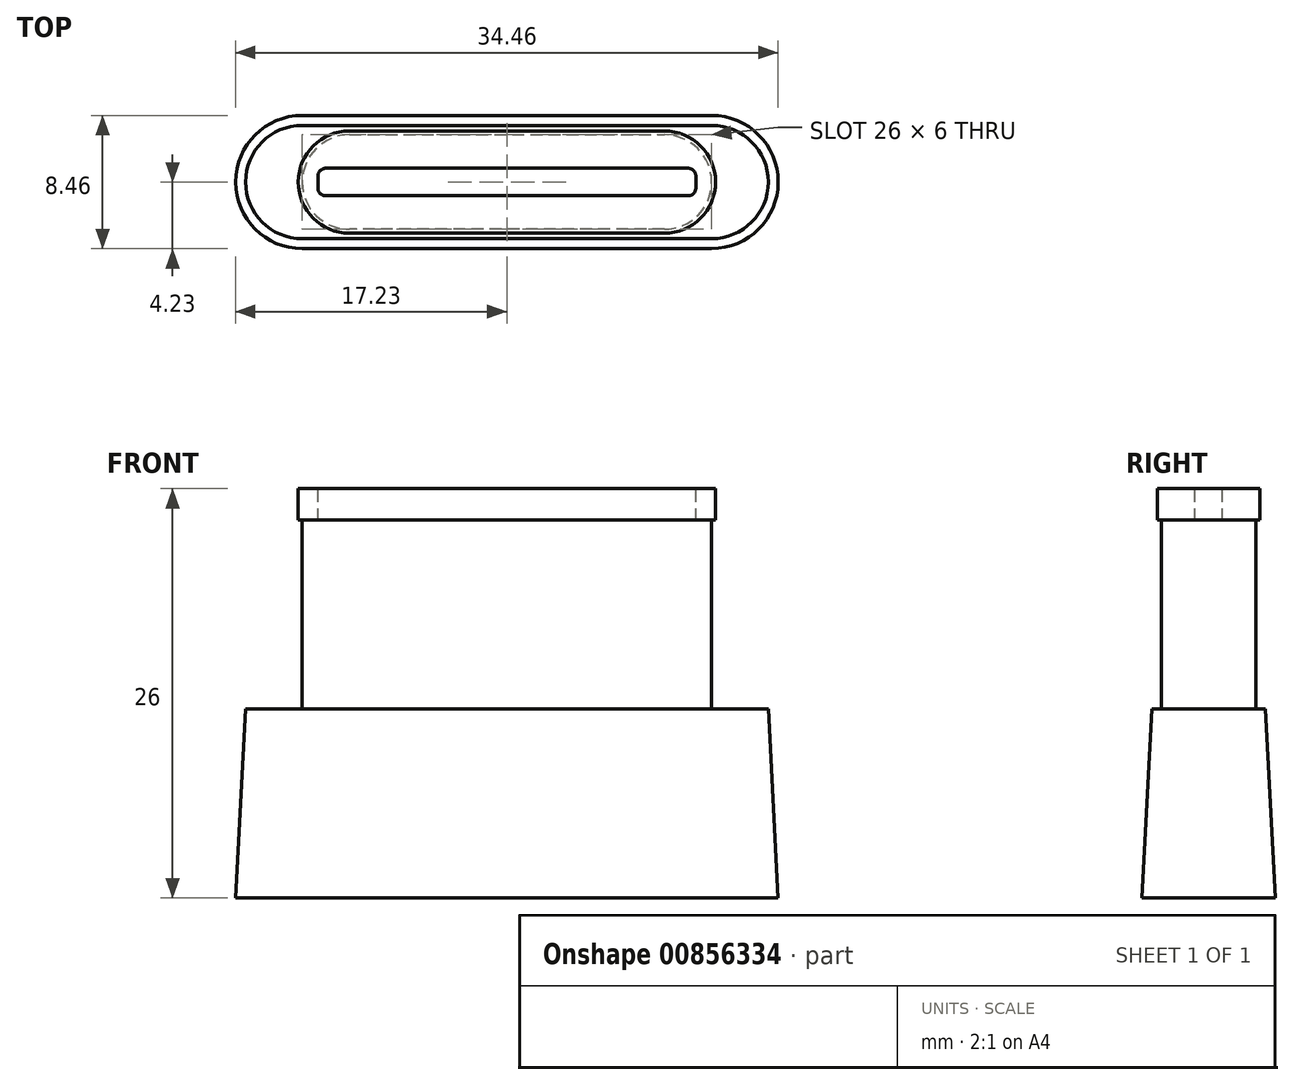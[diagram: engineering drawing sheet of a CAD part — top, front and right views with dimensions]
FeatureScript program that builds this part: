
annotation { "Feature Type Name" : "Feature", "Feature Type Description" : "" }
export const myFeature = defineFeature(function(context is Context, id is Id, definition is map)
    precondition{}
    {
        {
            var Q0;
            Q0=qCreatedBy(makeId("Top.planeOp"),FACE);
            var sketch = newSketch(context, id + "F0", { "sketchPlane" : qUnion([Q0])});
            skLineSegment(sketch, "E0.bottom", {"start": v(2.5, 0) * mm, "end": v(22.5, 0) * mm});
            skLineSegment(sketch, "E0.top", {"start": v(2.5, 5) * mm, "end": v(22.5, 5) * mm});
            skLineSegment(sketch, "E0.left", {"start": v(0, 2.5) * mm, "end": v(0, 2.5) * mm});
            skLineSegment(sketch, "E0.right", {"start": v(25, 2.5) * mm, "end": v(25, 2.5) * mm});
            skPoint(sketch, "E1.visualSharp", {"position": v(0, 5) * mm});
            skArc(sketch, "E1.filletArc", {"start": v(2.5, 5) * mm, "mid": v(0.73, 4.27) * mm, "end": v(0, 2.5) * mm});
            skPoint(sketch, "E2.visualSharp", {"position": v(0, 0) * mm});
            skArc(sketch, "E2.filletArc", {"start": v(0, 2.5) * mm, "mid": v(0.73, 0.73) * mm, "end": v(2.5, 0) * mm});
            skPoint(sketch, "E3.visualSharp", {"position": v(25, 5) * mm});
            skArc(sketch, "E3.filletArc", {"start": v(25, 2.5) * mm, "mid": v(24.27, 4.27) * mm, "end": v(22.5, 5) * mm});
            skPoint(sketch, "E4.visualSharp", {"position": v(25, 0) * mm});
            skArc(sketch, "E4.filletArc", {"start": v(22.5, 0) * mm, "mid": v(24.27, 0.73) * mm, "end": v(25, 2.5) * mm});
            skSolve(sketch);
        }
        {
            var Q0;
            Q0=makeQuery(id+"F0.imprint","IMPRINT",FACE,{"disambiguationData":[TD([[makeQuery(id+"F0.imprint","IMPRINT",EDGE,{"derivedFrom":sQuery(id+"F0.wireOp",EDGE,"E0.bottom")}),1.0]])]});
            extrude(context, id + "F1", {"entities" : qUnion([Q0]), "oppositeDirection" : true, "depth" : 2 * mm, "offsetDistance" : 25 * mm});
        }
        {
            var Q0;
            Q0=makeQuery(id+"F1.opExtrude","CAP_FACE",FACE,{"disambiguationData":[OSD([sQuery(id+"F0.wireOp",EDGE,"E0.bottom"),sQuery(id+"F0.wireOp",EDGE,"E0.top"),sQuery(id+"F0.wireOp",EDGE,"E0.left"),sQuery(id+"F0.wireOp",EDGE,"E0.right"),sQuery(id+"F0.wireOp",EDGE,"E1.filletArc"),sQuery(id+"F0.wireOp",EDGE,"E2.filletArc"),sQuery(id+"F0.wireOp",EDGE,"E3.filletArc"),sQuery(id+"F0.wireOp",EDGE,"E4.filletArc")])],"isStart":false});
            var sketch = newSketch(context, id + "F2", { "sketchPlane" : qUnion([Q0])});
            skArc(sketch, "E5.0", {"start": v(-0.5, -2.5) * mm, "mid": v(0.38, -4.62) * mm, "end": v(2.5, -5.5) * mm});
            skLineSegment(sketch, "E5.1", {"start": v(-0.5, -2.5) * mm, "end": v(-0.5, -2.5) * mm});
            skLineSegment(sketch, "E5.2", {"start": v(2.5, -5.5) * mm, "end": v(22.5, -5.5) * mm});
            skArc(sketch, "E5.3", {"start": v(2.5, 0.5) * mm, "mid": v(0.38, -0.38) * mm, "end": v(-0.5, -2.5) * mm});
            skArc(sketch, "E5.4", {"start": v(22.5, -5.5) * mm, "mid": v(24.62, -4.62) * mm, "end": v(25.5, -2.5) * mm});
            skLineSegment(sketch, "E5.5", {"start": v(25.5, -2.5) * mm, "end": v(25.5, -2.5) * mm});
            skArc(sketch, "E5.6", {"start": v(25.5, -2.5) * mm, "mid": v(24.62, -0.38) * mm, "end": v(22.5, 0.5) * mm});
            skLineSegment(sketch, "E5.7", {"start": v(22.5, 0.5) * mm, "end": v(2.5, 0.5) * mm});
            skSolve(sketch);
        }
        {
            var Q0;
            Q0=makeQuery(id+"F2.imprint","IMPRINT",FACE,{"disambiguationData":[TD([[makeQuery(id+"F2.imprint","IMPRINT",EDGE,{"derivedFrom":sQuery(id+"F2.wireOp",EDGE,"E5.0")}),1.0]])]});
            var Q1;
            Q1=makeQuery(id+"F2.imprint","IMPRINT",FACE,{"disambiguationData":[TD([[makeQuery(id+"F2.imprint","IMPRINT",EDGE,{"derivedFrom":makeQuery(id+"F1.opExtrude","CAP_EDGE",EDGE,{"disambiguationData":[OSD([sQuery(id+"F0.wireOp",EDGE,"E0.bottom")])],"isStart":false})}),-1.0]])]});
            extrude(context, id + "F3", {"entities" : qUnion([Q0, Q1]), "operationType" : NewBodyOperationType.ADD, "depth" : 12 * mm, "offsetDistance" : 25 * mm});
        }
        {
            var Q0;
            Q0=makeQuery(id+"F3.opExtrude","CAP_FACE",FACE,{"disambiguationData":[OSD([sQuery(id+"F2.wireOp",EDGE,"E5.0"),sQuery(id+"F2.wireOp",EDGE,"E5.2"),sQuery(id+"F2.wireOp",EDGE,"E5.3"),sQuery(id+"F2.wireOp",EDGE,"E5.4"),sQuery(id+"F2.wireOp",EDGE,"E5.6"),sQuery(id+"F2.wireOp",EDGE,"E5.7")])],"isStart":false});
            var sketch = newSketch(context, id + "F4", { "sketchPlane" : qUnion([Q0])});
            skLineSegment(sketch, "E6", {"start": v(-3.5, -2.5) * mm, "end": v(-3.5, -2.5) * mm});
            skLineSegment(sketch, "E7", {"start": v(28.5, -2.5) * mm, "end": v(28.5, -2.5) * mm});
            skLineSegment(sketch, "E8", {"start": v(-0.5, 0.5) * mm, "end": v(25.5, 0.5) * mm});
            skLineSegment(sketch, "E9", {"start": v(25.5, -5.5) * mm, "end": v(-0.5, -5.5) * mm});
            skPoint(sketch, "E10.visualSharp", {"position": v(-3.5, 0.5) * mm});
            skArc(sketch, "E10.filletArc", {"start": v(-0.5, 0.5) * mm, "mid": v(-2.62, -0.38) * mm, "end": v(-3.5, -2.5) * mm});
            skPoint(sketch, "E11.visualSharp", {"position": v(-3.5, -5.5) * mm});
            skArc(sketch, "E11.filletArc", {"start": v(-3.5, -2.5) * mm, "mid": v(-2.62, -4.62) * mm, "end": v(-0.5, -5.5) * mm});
            skPoint(sketch, "E12.visualSharp", {"position": v(28.5, 0.5) * mm});
            skArc(sketch, "E12.filletArc", {"start": v(28.5, -2.5) * mm, "mid": v(27.62, -0.38) * mm, "end": v(25.5, 0.5) * mm});
            skPoint(sketch, "E13.visualSharp", {"position": v(28.5, -5.5) * mm});
            skArc(sketch, "E13.filletArc", {"start": v(25.5, -5.5) * mm, "mid": v(27.62, -4.62) * mm, "end": v(28.5, -2.5) * mm});
            skArc(sketch, "E14.0", {"start": v(-0.5, 1.1) * mm, "mid": v(-3.05, 0.05) * mm, "end": v(-4.1, -2.5) * mm});
            skArc(sketch, "E14.1", {"start": v(29.1, -2.5) * mm, "mid": v(28.05, 0.05) * mm, "end": v(25.5, 1.1) * mm});
            skArc(sketch, "E14.2", {"start": v(25.5, -6.1) * mm, "mid": v(28.05, -5.05) * mm, "end": v(29.1, -2.5) * mm});
            skLineSegment(sketch, "E14.3", {"start": v(-0.5, 1.1) * mm, "end": v(25.5, 1.1) * mm});
            skLineSegment(sketch, "E14.4", {"start": v(25.5, -6.1) * mm, "end": v(-0.5, -6.1) * mm});
            skArc(sketch, "E14.5", {"start": v(-4.1, -2.5) * mm, "mid": v(-3.05, -5.05) * mm, "end": v(-0.5, -6.1) * mm});
            skSolve(sketch);
        }
        {
            var Q0;
            {var subQ1=sQuery(id+"F4.wireOp",EDGE,"E10.filletArc");Q0=makeQuery(id+"F4.imprint","IMPRINT",FACE,{"disambiguationData":[TD([[makeQuery(id+"F4.imprint","IMPRINT",EDGE,{"derivedFrom":subQ1}),1.0]])]});}
            var Q1;
            {var subQ1=makeQuery(id+"F3.opExtrude","CAP_EDGE",EDGE,{"disambiguationData":[OSD([sQuery(id+"F2.wireOp",EDGE,"E5.0"),sQuery(id+"F2.wireOp",EDGE,"E5.3")])],"isStart":false});Q1=makeQuery(id+"F4.imprint","IMPRINT",FACE,{"disambiguationData":[TD([[makeQuery(id+"F4.imprint","IMPRINT",EDGE,{"derivedFrom":subQ1}),1.0]])]});}
            var Q2;
            {var subQ1=sQuery(id+"F4.wireOp",EDGE,"E12.filletArc");Q2=makeQuery(id+"F4.imprint","IMPRINT",FACE,{"disambiguationData":[TD([[makeQuery(id+"F4.imprint","IMPRINT",EDGE,{"derivedFrom":subQ1}),1.0]])]});}
            var Q3;
            {var subQ3=sQuery(id+"F4.wireOp",EDGE,"E10.filletArc");Q3=makeQuery(id+"F4.imprint","IMPRINT",FACE,{"disambiguationData":[TD([[makeQuery(id+"F4.imprint","IMPRINT",EDGE,{"derivedFrom":subQ3}),-1.0]])]});}
            extrude(context, id + "F5", {"entities" : qUnion([Q0, Q1, Q2, Q3]), "operationType" : NewBodyOperationType.ADD, "depth" : 12 * mm, "offsetDistance" : 25 * mm, "hasDraft" : true, "draftAngle" : 3 * degree});
        }
        {
            var Q0;
            Q0=makeQuery(id+"F1.opExtrude","CAP_FACE",FACE,{"disambiguationData":[OSD([sQuery(id+"F0.wireOp",EDGE,"E0.bottom"),sQuery(id+"F0.wireOp",EDGE,"E0.top"),sQuery(id+"F0.wireOp",EDGE,"E1.filletArc"),sQuery(id+"F0.wireOp",EDGE,"E2.filletArc"),sQuery(id+"F0.wireOp",EDGE,"E3.filletArc"),sQuery(id+"F0.wireOp",EDGE,"E4.filletArc")])],"isStart":true});
            var sketch = newSketch(context, id + "F6", { "sketchPlane" : qUnion([Q0])});
            skLineSegment(sketch, "E15.bottom", {"start": v(0.5, 3.38) * mm, "end": v(24.5, 3.37) * mm});
            skLineSegment(sketch, "E15.top", {"start": v(0.5, 1.62) * mm, "end": v(24.5, 1.62) * mm});
            skLineSegment(sketch, "E15.left", {"start": v(0.5, 3.37) * mm, "end": v(0.5, 1.62) * mm});
            skLineSegment(sketch, "E15.right", {"start": v(24.5, 3.37) * mm, "end": v(24.5, 1.63) * mm});
            skLineSegment(sketch, "E16.0.0", {"start": v(22.5, 5) * mm, "end": v(2.5, 5) * mm});
            skArc(sketch, "E16.0.1", {"start": v(2.5, 5) * mm, "mid": v(0, 2.5) * mm, "end": v(2.5, 0) * mm});
            skLineSegment(sketch, "E16.0.2", {"start": v(2.5, 0) * mm, "end": v(22.5, 0) * mm});
            skArc(sketch, "E16.0.3", {"start": v(22.5, 0) * mm, "mid": v(25, 2.5) * mm, "end": v(22.5, 5) * mm});
            skLineSegment(sketch, "E17", {"start": v(0.5, 2.5) * mm, "end": v(24.5, 2.5) * mm, "construction": true});
            skLineSegment(sketch, "E18", {"start": v(12.5, 5) * mm, "end": v(12.5, 0) * mm, "construction": true});
            skLineSegment(sketch, "E19", {"start": v(12.5, 3.37) * mm, "end": v(12.5, 1.62) * mm, "construction": true});
            skSolve(sketch);
        }
        {
            var Q0;
            Q0=makeQuery(id+"F6.imprint","IMPRINT",FACE,{"disambiguationData":[TD([[makeQuery(id+"F6.imprint","IMPRINT",EDGE,{"derivedFrom":sQuery(id+"F6.wireOp",EDGE,"E15.bottom")}),-1.0]])]});
            extrude(context, id + "F7", {"entities" : qUnion([Q0]), "operationType" : NewBodyOperationType.REMOVE, "oppositeDirection" : true, "depth" : 2 * mm, "offsetDistance" : 25 * mm});
        }
        {
            var Q0;
            Q0=makeQuery(id+"F7.boolean.opBoolean","COPY",EDGE,{"derivedFrom":makeQuery(id+"F7.opExtrude","SWEPT_EDGE",EDGE,{"disambiguationData":[OSD([sQuery(id+"F6.wireOp",EDGE,"E15.bottom"),sQuery(id+"F6.wireOp",EDGE,"E15.left")])]})});
            var Q1;
            Q1=makeQuery(id+"F7.boolean.opBoolean","COPY",EDGE,{"derivedFrom":makeQuery(id+"F7.opExtrude","SWEPT_EDGE",EDGE,{"disambiguationData":[OSD([sQuery(id+"F6.wireOp",EDGE,"E15.top"),sQuery(id+"F6.wireOp",EDGE,"E15.left")])]})});
            var Q2;
            Q2=makeQuery(id+"F7.boolean.opBoolean","COPY",EDGE,{"derivedFrom":makeQuery(id+"F7.opExtrude","SWEPT_EDGE",EDGE,{"disambiguationData":[OSD([sQuery(id+"F6.wireOp",EDGE,"E15.top"),sQuery(id+"F6.wireOp",EDGE,"E15.right")])]})});
            var Q3;
            Q3=makeQuery(id+"F7.boolean.opBoolean","COPY",EDGE,{"derivedFrom":makeQuery(id+"F7.opExtrude","SWEPT_EDGE",EDGE,{"disambiguationData":[OSD([sQuery(id+"F6.wireOp",EDGE,"E15.bottom"),sQuery(id+"F6.wireOp",EDGE,"E15.right")])]})});
            fillet(context, id + "F8", {"entities" : qUnion([Q0, Q1, Q2, Q3]), "radius" : 0.5 * mm, "tangentPropagation" : true, "allowEdgeOverflow" : false});
        }
        {
            var Q0;
            Q0=makeQuery(id+"F1.opExtrude","CAP_FACE",FACE,{"disambiguationData":[OSD([sQuery(id+"F0.wireOp",EDGE,"E0.bottom"),sQuery(id+"F0.wireOp",EDGE,"E0.top"),sQuery(id+"F0.wireOp",EDGE,"E1.filletArc"),sQuery(id+"F0.wireOp",EDGE,"E2.filletArc"),sQuery(id+"F0.wireOp",EDGE,"E3.filletArc"),sQuery(id+"F0.wireOp",EDGE,"E4.filletArc")])],"isStart":true});
            var Q1;
            Q1=makeQuery(id+"F1.opExtrude","CAP_FACE",FACE,{"disambiguationData":[OSD([sQuery(id+"F0.wireOp",EDGE,"E0.bottom"),sQuery(id+"F0.wireOp",EDGE,"E0.top"),sQuery(id+"F0.wireOp",EDGE,"E1.filletArc"),sQuery(id+"F0.wireOp",EDGE,"E2.filletArc"),sQuery(id+"F0.wireOp",EDGE,"E3.filletArc"),sQuery(id+"F0.wireOp",EDGE,"E4.filletArc")])],"isStart":true});
            var sketch = newSketch(context, id + "F9", { "sketchPlane" : qUnion([Q0, Q1])});
            skArc(sketch, "E20.0", {"start": v(2.5, 5.75) * mm, "mid": v(-0.75, 2.5) * mm, "end": v(2.5, -0.75) * mm});
            skLineSegment(sketch, "E20.1", {"start": v(2.5, 5.75) * mm, "end": v(22.5, 5.75) * mm});
            skArc(sketch, "E20.2", {"start": v(22.5, -0.75) * mm, "mid": v(25.75, 2.5) * mm, "end": v(22.5, 5.75) * mm});
            skLineSegment(sketch, "E20.3", {"start": v(2.5, -0.75) * mm, "end": v(22.5, -0.75) * mm});
            skSolve(sketch);
        }
        {
            var Q0;
            Q0=makeQuery(id+"F9.imprint","IMPRINT",FACE,{"disambiguationData":[TD([[makeQuery(id+"F9.imprint","IMPRINT",EDGE,{"derivedFrom":sQuery(id+"F9.wireOp",EDGE,"E20.0")}),1.0]])]});
            extrude(context, id + "F10", {"entities" : qUnion([Q0]), "operationType" : NewBodyOperationType.ADD, "oppositeDirection" : true, "depth" : 2 * mm, "offsetDistance" : 25 * mm});
        }
    });
